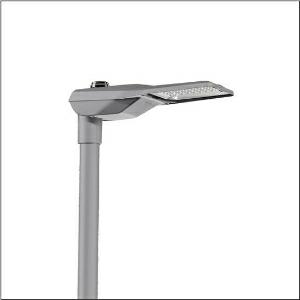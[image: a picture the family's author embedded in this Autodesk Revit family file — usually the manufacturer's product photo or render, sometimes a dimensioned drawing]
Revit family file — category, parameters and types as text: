
# Revit family: streetlight_sl_21_mini___st1_0a_5xe6d27n08hb_8446
name_source: partatom
category: Lighting Fixtures
units: mm (PartAtom-declared; Revit-internal decimal feet)

## family parameters
Cut with Voids When Loaded = No
Host = Face
Light Source = No
Part Type = Normal
Room Calculation Point = No
Round Connector Dimension = Use Diameter
Shared = No

## types (1)
- --- (1 x LED, 7490 lm, 66 W, 2200K)
    Apparent Load = 66 VA
    CIE Flux Codes = 37 72 97 100 100
    Color Rendering = 70
    Color Temperature = 2200K
    Default Elevation = 1800 mm
    Description = Streetlight SL 21 mini, mast luminaire, primary light control with lens, of PMMA, primary optical cover: cover, of toughened safety glass, transparent, light distribution: ST1.0a, light emission: direct distribution, primary light characteristic: asymmetric, installation type: side-entry, LED, 3G 1.5mm², High Power LED, rated luminous flux: 7.490lm, luminous efficacy: 114lm/W, light colour: 722, colour temperature: 2200K, control gear: NEMA (7pin), control: overheat protection, pre-setting: linear dimming characteristic, constant luminous flux control, time-dependent luminous flux control, flexible luminous flux parameterisation, mains connection: 230..240V, AC, 50/60Hz, connection cable pre-assembled, cable length: 8,5m, wiring characteristics: H07RN-F, start of lifetime: 66W, end of service life: 69W, reduction: 30W, luminaire housing, of diecast aluminium (EN AC-44300), powder-coated, Siteco® metallic grey (DB 702S), corrosivity category C5 mid according to DIN EN ISO 12944, multi-level sealing system, sealing non-destructively replaceable, inclination adjustable: 0°, 5°, 10°, 15°, length: 628mm, width: 235mm, height: 110mm, spigot size: 42mm (side-entry), mounting height: 4..8m, protection rating (complete): IP66, insulation class (complete): insulation class I (protective earthing), certification: CE, ENEC, ENEC+, VDE, impact resistance: IK10, permissible operating ambient temperature for outdoor applications: -40..+50°C, standard-compliant lighting for roads and squares, packaging unit: 1 piece

Light Distribution: ST1.0a
    Height = 110 mm
    Lamp = 1 x LED
    Lamp Light Flux = 7490 lm
    Lamp Power = 66 W
    Lamp count = 1
    Length = 625 mm
    Luminous efficacy = 113 lm/W
    Manufacturer = Siteco
    ModVariant = No
    Model = 5XE6D27N08HB
    Number of Poles = 1
    OnlyDefault = Yes
    Power Factor = 1
    Product Name = Streetlight SL 21 mini | ST1.0a
    Product group = mast luminaire | pylon top
    ProductGroupID = 6100
    Protection Class = Protection class I
    Protection Degree = IP 66
    RLX_Detail_Level = 1
    RLX_Emergency_Light_Flux = 0 lm
    RLX_Emergency_Type = 0
    RLX_Emergency_Type_DB = No
    RlxData = <blob elided: 26105 chars, md5=8ce90482>
    Socket = socket
    Standby Power = 0 W
    System Light Flux = 7490 lm
    System Power = 66 W
    Type Comments = factory setting: luminous flux: 100 % | dim-lin: 254 | 670 mA
    Type Image = l_1294379.jpg
    URL = http://relux.com
    VarID = @adj_157839
    Voltage = 0 V
    Weight = 0.00 kg
    Width = 234 mm

## geometry (parser evidence)
native form markers: Blend x4, Sweep x9
no freeform markers — native parametric forms only
